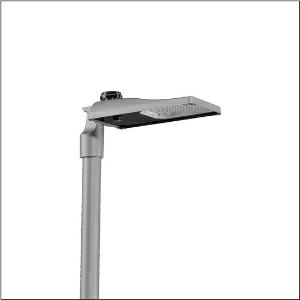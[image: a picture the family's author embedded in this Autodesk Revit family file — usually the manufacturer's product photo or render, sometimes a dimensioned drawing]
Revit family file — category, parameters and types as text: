
# Revit family: streetlight_sl_31_mini___st1_0a_5xh6d35m08ga_0c89
name_source: partatom
category: Lighting Fixtures
units: mm (PartAtom-declared; Revit-internal decimal feet)

## family parameters
Cut with Voids When Loaded = No
Host = Face
Light Source = No
Part Type = Normal
Room Calculation Point = No
Round Connector Dimension = Use Diameter
Shared = No

## types (1)
- --- (1 x LED, 5880 lm, 39.3 W, 3000K)
    Apparent Load = 39 VA
    CIE Flux Codes = 37 72 97 100 100
    Color Rendering = 70
    Color Temperature = 3000K
    Default Elevation = 1800 mm
    Description = Streetlight SL 31 mini, mast luminaire, primary light control with lens, of PMMA, primary optical cover: cover, of toughened safety glass, transparent, light distribution: ST1.0a, light emission: direct distribution, primary light characteristic: asymmetric, installation type: post-top, side-entry, LED, High Power LED, rated luminous flux: 5.880lm, luminous efficacy: 150lm/W, light colour: 730, colour temperature: 3000K, control: presetting dimming linear, flexible luminous flux parameterisation, time-dependent luminous flux control, constant luminous flux control, intelligent temperature release in ECG and LED module, overheat protection, with cable H07RN-F 3x 1.5mm², mains connection: 220..240V, AC, 50/60Hz, connection cable pre-assembled, cable length: 6,5m, start of lifetime: 39W, end of service life: 41W, reduction: 18W, luminaire housing, of diecast aluminium, powder-coated, Siteco® metallic grey (DB 702S), corrosivity category C5 high according to DIN EN ISO 12944, no sealing on luminaire upper side, inclination: -15°..+20° (post-top) | -20°..+20° (side-entry), adjustable in 5° steps, mast flange (76/60mm) included as standard, multi-level sealing system, sealing non-destructively replaceable, Smart Interface below, protection rating (complete): IP66, insulation class (complete): insulation class I (protective earthing), certification: CE, ENEC, ENEC+, VDE, UKCA, impact resistance: IK09, permissible operating ambient temperature for outdoor applications: -40..+50°C, standard-compliant lighting for roads and squares, packaging unit: 1 piece

Light Distribution: ST1.0a
    Height = 76 mm
    Lamp = 1 x LED
    Lamp Light Flux = 5880 lm
    Lamp Power = 39.3 W
    Lamp count = 1
    Length = 547 mm
    Luminous efficacy = 150 lm/W
    Manufacturer = Siteco
    ModVariant = No
    Model = 5XH6D35M08GA
    Number of Poles = 1
    OnlyDefault = Yes
    Power Factor = 1
    Product Name = Streetlight SL 31 mini | ST1.0a
    Product group = mast luminaire | pylon top
    ProductGroupID = 6100
    Protection Class = Protection class I
    Protection Degree = IP 66
    RLX_Detail_Level = 1
    RLX_Emergency_Light_Flux = 0 lm
    RLX_Emergency_Type = 0
    RLX_Emergency_Type_DB = No
    RlxData = <blob elided: 40561 chars, md5=823d6684>
    Socket = socket
    Standby Power = 0 W
    System Light Flux = 5880 lm
    System Power = 39 W
    Type Comments = factory setting: luminous flux: 100 % | dim-lin: 254 | 798 mA
    Type Image = l_1300324.jpg
    URL = http://relux.com
    VarID = @adj_011403
    Voltage = 0 V
    Weight = 0.00 kg
    Width = 265 mm

## geometry (parser evidence)
native form markers: Blend x4, Sweep x10
no freeform markers — native parametric forms only
